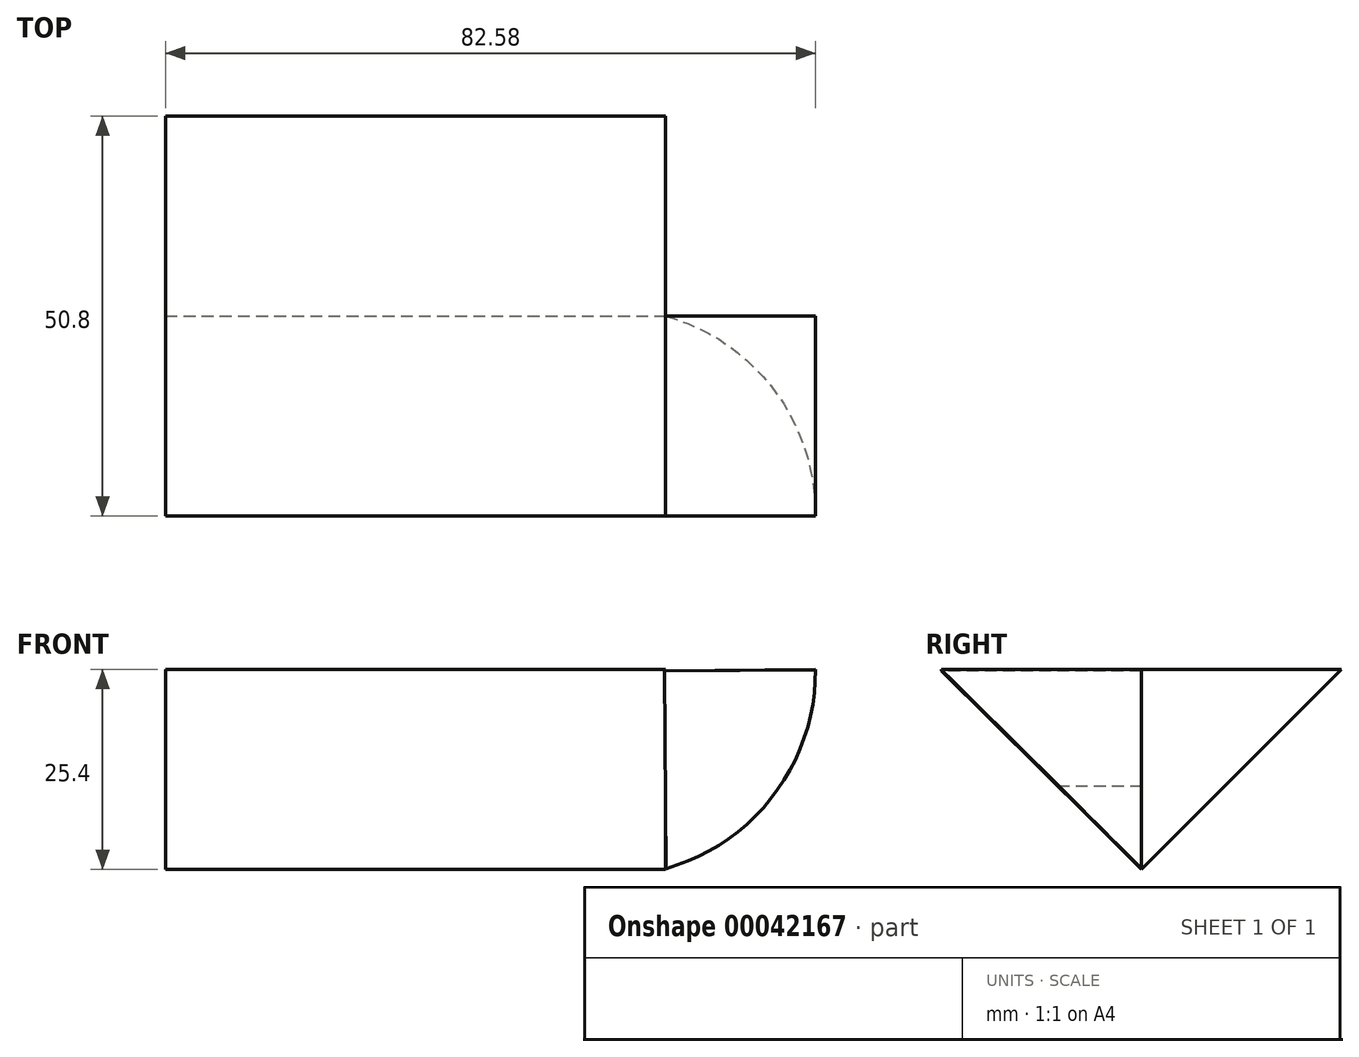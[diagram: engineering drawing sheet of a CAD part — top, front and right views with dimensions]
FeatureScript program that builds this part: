
annotation { "Feature Type Name" : "Feature", "Feature Type Description" : "" }
export const myFeature = defineFeature(function(context is Context, id is Id, definition is map)
    precondition{}
    {
        {
            var Q0;
            Q0=qCreatedBy(makeId("Top.planeOp"),FACE);
            var sketch = newSketch(context, id + "F0", { "sketchPlane" : qUnion([Q0])});
            skLineSegment(sketch, "E0.rect.bottom", {"start": v(-31.75, 38.1) * mm, "end": v(31.75, 38.1) * mm});
            skLineSegment(sketch, "E0.rect.top", {"start": v(-31.75, -38.1) * mm, "end": v(31.75, -38.1) * mm});
            skLineSegment(sketch, "E0.rect.left", {"start": v(-31.75, 38.1) * mm, "end": v(-31.75, -38.1) * mm});
            skLineSegment(sketch, "E0.rect.right", {"start": v(31.75, 38.1) * mm, "end": v(31.75, -38.1) * mm});
            skPoint(sketch, "E0.rect.middle", {"position": v(0, 0) * mm});
            skSolve(sketch);
        }
        {
            var Q0;
            Q0=makeQuery(id+"F0.imprint","IMPRINT",FACE,{"disambiguationData":[TD([[makeQuery(id+"F0.imprint","IMPRINT",EDGE,{"derivedFrom":sQuery(id+"F0.wireOp",EDGE,"E0.rect.bottom")}),-1.0]])]});
            extrude(context, id + "F1", {"entities" : qUnion([Q0]), "oppositeDirection" : true, "depth" : 25.4 * mm});
        }
        {
            var Q0;
            Q0=makeQuery(id+"F1.opExtrude","CAP_EDGE",EDGE,{"disambiguationData":[OSD([sQuery(id+"F0.wireOp",EDGE,"E0.rect.bottom")])],"isStart":false});
            chamfer(context, id + "F2", {"entities" : qUnion([Q0]), "width" : 38.1 * mm, "tangentPropagation" : true});
        }
        {
            var Q0;
            Q0=makeQuery(id+"F1.opExtrude","CAP_EDGE",EDGE,{"disambiguationData":[OSD([sQuery(id+"F0.wireOp",EDGE,"E0.rect.top")])],"isStart":false});
            chamfer(context, id + "F3", {"entities" : qUnion([Q0]), "width" : 38.1 * mm, "tangentPropagation" : true});
        }
        {
            var Q0;
            Q0=qCreatedBy(makeId("Front.planeOp"),FACE);
            var sketch = newSketch(context, id + "F4", { "sketchPlane" : qUnion([Q0])});
            skArc(sketch, "E1", {"start": v(31.84, -25.32) * mm, "mid": v(45.6, -15.86) * mm, "end": v(50.83, 0) * mm});
            skLineSegment(sketch, "E2", {"start": v(50.83, 0) * mm, "end": v(31.62, -0.2) * mm});
            skLineSegment(sketch, "E3", {"start": v(31.62, -0.2) * mm, "end": v(31.84, -25.32) * mm});
            skSolve(sketch);
        }
        {
            var Q0;
            Q0=makeQuery(id+"F4.imprint","IMPRINT",FACE,{"disambiguationData":[TD([[makeQuery(id+"F4.imprint","IMPRINT",EDGE,{"derivedFrom":sQuery(id+"F4.wireOp",EDGE,"E1")}),1.0]])]});
            extrude(context, id + "F5", {"entities" : qUnion([Q0]), "operationType" : NewBodyOperationType.ADD, "depth" : 25.4 * mm});
        }
        {
            var Q0;
            Q0=makeQuery(id+"F5.opExtrude","SWEPT_FACE",FACE,{"disambiguationData":[OSD([sQuery(id+"F4.wireOp",EDGE,"E3")])]});
            var sketch = newSketch(context, id + "F6", { "sketchPlane" : qUnion([Q0])});
            skLineSegment(sketch, "E4", {"start": v(0, -25.6) * mm, "end": v(25.4, -0.47) * mm});
            skLineSegment(sketch, "E5", {"start": v(25.4, -0.47) * mm, "end": v(25.4, -25.6) * mm});
            skLineSegment(sketch, "E6", {"start": v(25.4, -25.6) * mm, "end": v(0, -25.6) * mm});
            skSolve(sketch);
        }
        {
            var Q0;
            Q0=makeQuery(id+"F6.imprint","IMPRINT",FACE,{"disambiguationData":[TD([[makeQuery(id+"F6.imprint","IMPRINT",EDGE,{"derivedFrom":sQuery(id+"F6.wireOp",EDGE,"E4")}),-1.0]])]});
            extrude(context, id + "F7", {"entities" : qUnion([Q0]), "operationType" : NewBodyOperationType.REMOVE, "oppositeDirection" : true, "depth" : 25.4 * mm});
        }
    });
